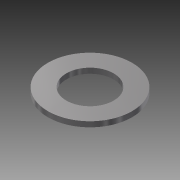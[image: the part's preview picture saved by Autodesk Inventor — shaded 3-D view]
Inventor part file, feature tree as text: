
AUTODESK INVENTOR PART (.ipt)
format: ipt  version: 2013 (Build 170138000, 138)  size: 78,848 bytes
history: native  units: mm
features: other x1, extrude x1, sketch x1
ambient origin geometry x1: Origin
feature tree (3):
  other  "ソリッド1"
  extrude  "押し出し1"  Depth=4.5mm
  sketch  "スケッチ1"
